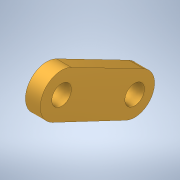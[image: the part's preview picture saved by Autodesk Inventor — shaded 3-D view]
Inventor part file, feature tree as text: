
AUTODESK INVENTOR PART (.ipt)
format: ipt  version: 2020 (Build 240168000, 168)  size: 142,848 bytes
history: native  units: in
note: dims shown in document units (in); Inventor stores cm internally (conversion verified against a paired STEP export)
features: extrude x3, sketch x3, projected_geometry x1
ambient origin geometry x8: Origin, YZ Plane, XZ Plane, XY Plane, X Axis, Y Axis, Z Axis, Center Point
bodies: Solid1 (feature_tree)
feature tree (7):
  extrude  "Extrusion1"  Depth=0.4523in
  extrude  "Extrusion2"  Depth=0.2118in
  extrude  "Extrusion3"  Depth=0.1575in TaperAngle=0.0deg
  sketch  "Sketch1"  dims[d0=0.2087in d1=0.2087in d3=0.4523in]
  sketch  "Sketch2"  dims[d4=0.2118in d5=0.8586in]
  projected_geometry  "Projected Loop1"
  sketch  "Sketch3"  dims[d6=0.8656in d7=0.1575in d8=0.0in d11=0.0787in d12=0.315in d13=0.1575in d14=0.0in d15=0.1969in d16=0.0787in d17=0.0in d20=0.7087in d21=0.4228in]
